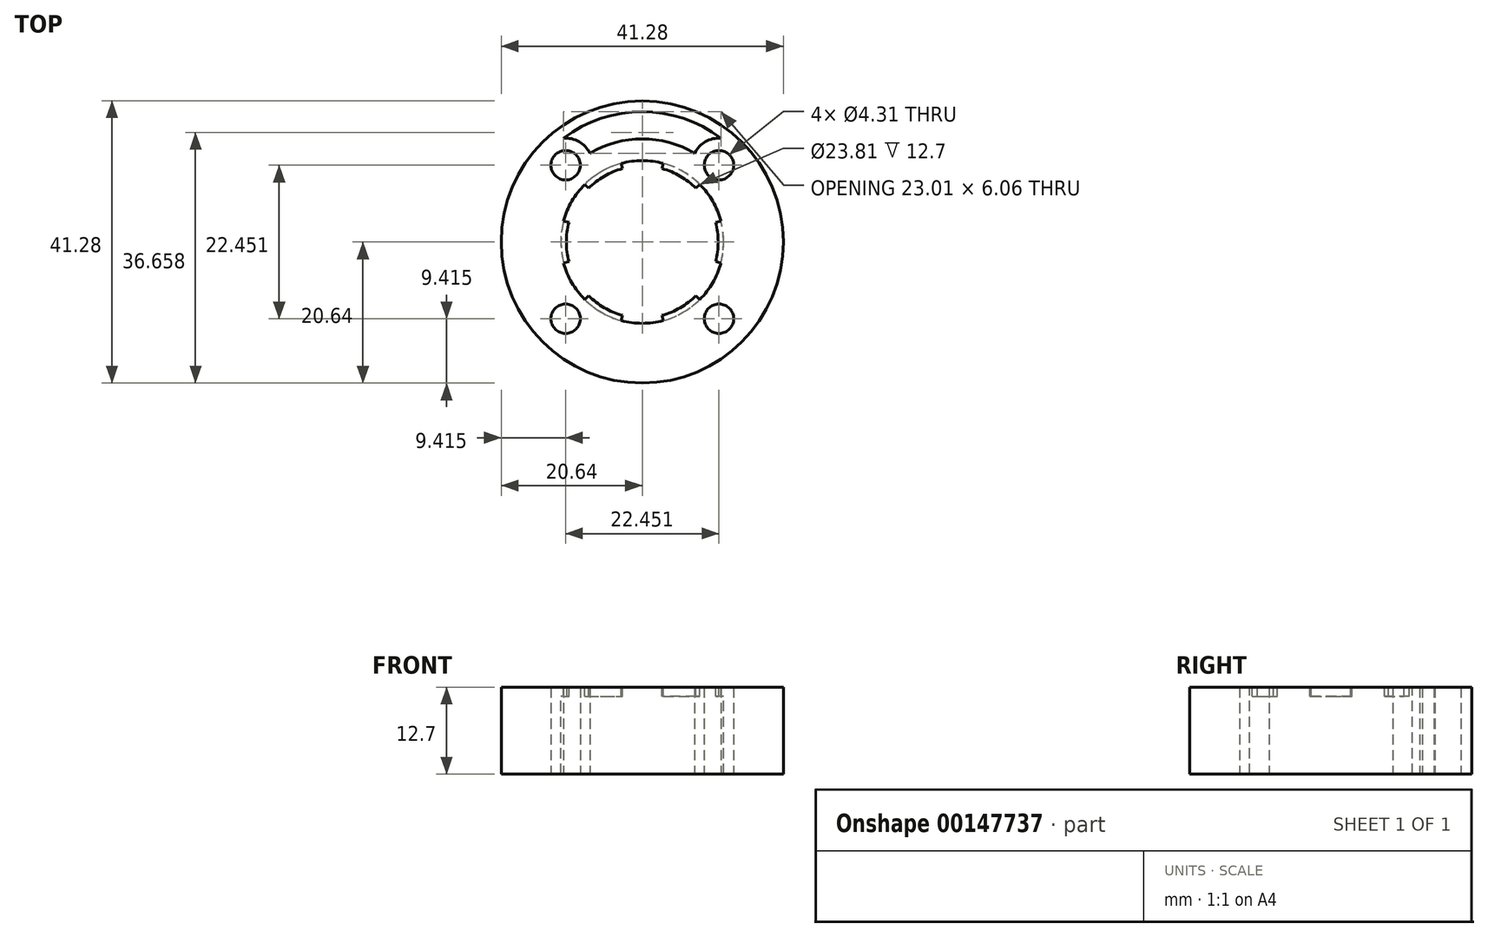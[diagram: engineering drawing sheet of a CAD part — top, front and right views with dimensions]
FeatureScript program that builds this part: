
annotation { "Feature Type Name" : "Feature", "Feature Type Description" : "" }
export const myFeature = defineFeature(function(context is Context, id is Id, definition is map)
    precondition{}
    {
        {
            var Q0;
            Q0=qCreatedBy(makeId("Top.planeOp"),FACE);
            var sketch = newSketch(context, id + "F0", { "sketchPlane" : qUnion([Q0])});
            skCircle(sketch, "E0", {"center": v(0, 0) * mm, "radius": 11.11 * mm});
            skLineSegment(sketch, "E1.bottom", {"start": v(11.23, 11.23) * mm, "end": v(-11.23, 11.23) * mm, "construction": true});
            skLineSegment(sketch, "E1.top", {"start": v(11.23, -11.23) * mm, "end": v(-11.23, -11.23) * mm, "construction": true});
            skLineSegment(sketch, "E1.left", {"start": v(11.23, 11.23) * mm, "end": v(11.23, -11.23) * mm, "construction": true});
            skLineSegment(sketch, "E1.right", {"start": v(-11.23, 11.23) * mm, "end": v(-11.23, -11.23) * mm, "construction": true});
            skCircle(sketch, "E2", {"center": v(-11.23, 11.23) * mm, "radius": 4.76 * mm, "construction": true});
            skLineSegment(sketch, "E3", {"start": v(0, 0) * mm, "end": v(0, 11.11) * mm});
            skCircle(sketch, "E4", {"center": v(-11.23, 11.23) * mm, "radius": 2.15 * mm});
            skCircle(sketch, "E5", {"center": v(-11.23, -11.23) * mm, "radius": 2.15 * mm});
            skCircle(sketch, "E6", {"center": v(11.23, -11.23) * mm, "radius": 2.15 * mm});
            skCircle(sketch, "E7", {"center": v(11.23, 11.23) * mm, "radius": 2.15 * mm});
            skCircle(sketch, "E8", {"center": v(0, 0) * mm, "radius": 20.64 * mm});
            skSolve(sketch);
        }
        {
            var Q0;
            Q0=qSketchRegion(id+"F0",true);
            extrude(context, id + "F1", {"entities" : qUnion([Q0]), "depth" : 12.7 * mm});
        }
        {
            var Q0;
            Q0=makeQuery(id+"F1.opExtrude","CAP_FACE",FACE,{"disambiguationData":[OSD([sQuery(id+"F0.wireOp",EDGE,"E0"),sQuery(id+"F0.wireOp",EDGE,"66XUYhlC-g5MV-aD6u-Z0ay-hjDTK084ohIY.top"),sQuery(id+"F0.wireOp",EDGE,"66XUYhlC-g5MV-aD6u-Z0ay-hjDTK084ohIY.left"),sQuery(id+"F0.wireOp",EDGE,"66XUYhlC-g5MV-aD6u-Z0ay-hjDTK084ohIY.right"),sQuery(id+"F0.wireOp",EDGE,"nqN0bBuQ-hJ1m-BtXy-d5jW-CiUxEReohyUV"),sQuery(id+"F0.wireOp",EDGE,"E4"),sQuery(id+"F0.wireOp",EDGE,"E5"),sQuery(id+"F0.wireOp",EDGE,"E6"),sQuery(id+"F0.wireOp",EDGE,"E7")])],"isStart":false});
            var sketch = newSketch(context, id + "F2", { "sketchPlane" : qUnion([Q0])});
            skLineSegment(sketch, "E9", {"start": v(0, 0) * mm, "end": v(0, 11.11) * mm, "construction": true});
            skLineSegment(sketch, "E10", {"start": v(0, 0) * mm, "end": v(2.88, 10.73) * mm, "construction": true});
            skLineSegment(sketch, "E11", {"start": v(0, 0) * mm, "end": v(-2.88, 10.73) * mm, "construction": true});
            skArc(sketch, "E12", {"start": v(2.88, 10.73) * mm, "mid": v(0, 11.11) * mm, "end": v(-2.88, 10.73) * mm});
            skLineSegment(sketch, "E13", {"start": v(-2.88, 10.73) * mm, "end": v(-3.08, 11.5) * mm});
            skLineSegment(sketch, "E14", {"start": v(2.88, 10.73) * mm, "end": v(3.08, 11.5) * mm});
            skArc(sketch, "E15", {"start": v(3.08, 11.5) * mm, "mid": v(0, 11.9) * mm, "end": v(-3.08, 11.5) * mm});
            skSolve(sketch);
        }
        {
            var Q0;
            Q0=qSketchRegion(id+"F2",true);
            var Q1;
            Q1=makeQuery(id+"F1.opExtrude","CAP_FACE",FACE,{"disambiguationData":[OSD([sQuery(id+"F0.wireOp",EDGE,"E0"),sQuery(id+"F0.wireOp",EDGE,"66XUYhlC-g5MV-aD6u-Z0ay-hjDTK084ohIY.top"),sQuery(id+"F0.wireOp",EDGE,"66XUYhlC-g5MV-aD6u-Z0ay-hjDTK084ohIY.left"),sQuery(id+"F0.wireOp",EDGE,"66XUYhlC-g5MV-aD6u-Z0ay-hjDTK084ohIY.right"),sQuery(id+"F0.wireOp",EDGE,"nqN0bBuQ-hJ1m-BtXy-d5jW-CiUxEReohyUV"),sQuery(id+"F0.wireOp",EDGE,"E4"),sQuery(id+"F0.wireOp",EDGE,"E5"),sQuery(id+"F0.wireOp",EDGE,"E6"),sQuery(id+"F0.wireOp",EDGE,"E7")])],"isStart":true});
            extrude(context, id + "F3", {"entities" : qUnion([Q0]), "operationType" : NewBodyOperationType.REMOVE, "endBound" : BoundingType.UP_TO_SURFACE, "oppositeDirection" : true, "endBoundEntityFace" : qUnion([Q1]), "depth" : 25.4 * mm});
        }
        {
            var Q0;
            Q0=makeQuery(id+"F3.boolean.opBoolean","COPY",FACE,{"derivedFrom":makeQuery(id+"F3.opExtrude","SWEPT_FACE",FACE,{"disambiguationData":[OSD([sQuery(id+"F2.wireOp",EDGE,"E15")])]})});
            var Q1;
            Q1=makeQuery(id+"F3.boolean.opBoolean","COPY",FACE,{"derivedFrom":makeQuery(id+"F3.opExtrude","SWEPT_FACE",FACE,{"disambiguationData":[OSD([sQuery(id+"F2.wireOp",EDGE,"E13")])]})});
            var Q2;
            Q2=makeQuery(id+"F3.boolean.opBoolean","COPY",FACE,{"derivedFrom":makeQuery(id+"F3.opExtrude","SWEPT_FACE",FACE,{"disambiguationData":[OSD([sQuery(id+"F2.wireOp",EDGE,"E14")])]})});
            var Q3;
            Q3=makeQuery(id+"F1.opExtrude","SWEPT_FACE",FACE,{"disambiguationData":[OSD([sQuery(id+"F0.wireOp",EDGE,"E0")])]});
            circularPattern(context, id + "F4", {"patternType" : PatternType.FACE, "faces" : qUnion([Q0, Q1, Q2]), "axis" : qUnion([Q3]), "angle" : 60 * degree, "instanceCount" : 6});
        }
        {
            var Q0;
            Q0=makeQuery(id+"F1.opExtrude","CAP_FACE",FACE,{"disambiguationData":[OSD([sQuery(id+"F0.wireOp",EDGE,"E0"),sQuery(id+"F0.wireOp",EDGE,"E4"),sQuery(id+"F0.wireOp",EDGE,"E5"),sQuery(id+"F0.wireOp",EDGE,"E6"),sQuery(id+"F0.wireOp",EDGE,"E7"),sQuery(id+"F0.wireOp",EDGE,"E8")])],"isStart":false});
            cPlane(context, id + "F5", {"entities" : qUnion([Q0]), "cplaneType" : CPlaneType.OFFSET, "offset" : 1.34 * mm, "oppositeDirection" : true, "width" : 152.4 * mm, "height" : 152.4 * mm});
        }
        {
            var Q0;
            Q0=makeQuery(id+"F1.opExtrude","CAP_FACE",FACE,{"disambiguationData":[OSD([sQuery(id+"F0.wireOp",EDGE,"E0"),sQuery(id+"F0.wireOp",EDGE,"E4"),sQuery(id+"F0.wireOp",EDGE,"E5"),sQuery(id+"F0.wireOp",EDGE,"E6"),sQuery(id+"F0.wireOp",EDGE,"E7"),sQuery(id+"F0.wireOp",EDGE,"E8")])],"isStart":true});
            var sketch = newSketch(context, id + "F6", { "sketchPlane" : qUnion([Q0])});
            skCircle(sketch, "E16", {"center": v(0, 0) * mm, "radius": 11.9 * mm});
            skSolve(sketch);
        }
        {
            var Q0;
            Q0=qSketchRegion(id+"F6",true);
            var Q1;
            Q1=qCreatedBy(id+"F5.planeOp",FACE);
            extrude(context, id + "F7", {"entities" : qUnion([Q0]), "operationType" : NewBodyOperationType.REMOVE, "endBound" : BoundingType.UP_TO_SURFACE, "oppositeDirection" : true, "endBoundEntityFace" : qUnion([Q1]), "depth" : 25.4 * mm});
        }
        {
            var Q0;
            Q0=makeQuery(id+"F1.opExtrude","CAP_FACE",FACE,{"disambiguationData":[OSD([sQuery(id+"F0.wireOp",EDGE,"E0"),sQuery(id+"F0.wireOp",EDGE,"E4"),sQuery(id+"F0.wireOp",EDGE,"E5"),sQuery(id+"F0.wireOp",EDGE,"E6"),sQuery(id+"F0.wireOp",EDGE,"E7"),sQuery(id+"F0.wireOp",EDGE,"E8")])],"isStart":true});
            var sketch = newSketch(context, id + "F8", { "sketchPlane" : qUnion([Q0])});
            skArc(sketch, "E17", {"start": v(7.67, -12.99) * mm, "mid": v(9.25, -14.67) * mm, "end": v(11.5, -15.18) * mm});
            skArc(sketch, "E18", {"start": v(-11.5, -15.18) * mm, "mid": v(0, -19.05) * mm, "end": v(11.5, -15.18) * mm});
            skArc(sketch, "E19", {"start": v(-7.67, -12.99) * mm, "mid": v(0, -15.08) * mm, "end": v(7.67, -12.99) * mm});
            skArc(sketch, "E20", {"start": v(-11.5, -15.18) * mm, "mid": v(-9.25, -14.67) * mm, "end": v(-7.67, -12.99) * mm});
            skSolve(sketch);
        }
        {
            var Q0;
            Q0=qSketchRegion(id+"F8",true);
            var Q1;
            Q1=makeQuery(id+"F1.opExtrude","CAP_FACE",FACE,{"disambiguationData":[OSD([sQuery(id+"F0.wireOp",EDGE,"E0"),sQuery(id+"F0.wireOp",EDGE,"E4"),sQuery(id+"F0.wireOp",EDGE,"E5"),sQuery(id+"F0.wireOp",EDGE,"E6"),sQuery(id+"F0.wireOp",EDGE,"E7"),sQuery(id+"F0.wireOp",EDGE,"E8")])],"isStart":false});
            extrude(context, id + "F9", {"entities" : qUnion([Q0]), "operationType" : NewBodyOperationType.REMOVE, "endBound" : BoundingType.UP_TO_SURFACE, "oppositeDirection" : true, "endBoundEntityFace" : qUnion([Q1]), "depth" : 25.4 * mm});
        }
    });
